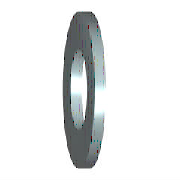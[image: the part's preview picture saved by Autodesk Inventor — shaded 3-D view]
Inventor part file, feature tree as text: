
AUTODESK INVENTOR PART (.ipt)
format: ipt  version: 2020 (Build 240168000, 168)  size: 110,592 bytes
history: native  units: mm (DEFAULTED — no unit token found)
features: other x1, plane x1, sketch x1
ambient origin geometry x7: Origin, YZ Plane, XY Plane, X Axis, Y Axis, Z Axis, Center Point
bodies: Solid1 (feature_tree), Body (feature_tree)
feature tree (3):
  other  "Work Axis1"
  plane  "Work Plane1"
  sketch  "Sketch"  dims[d0=6.4mm d1=12.0mm d2=1.6mm d3=0.0mm d4=0.0mm d5=0.0mm d6=0.0mm d7=0.0mm]
